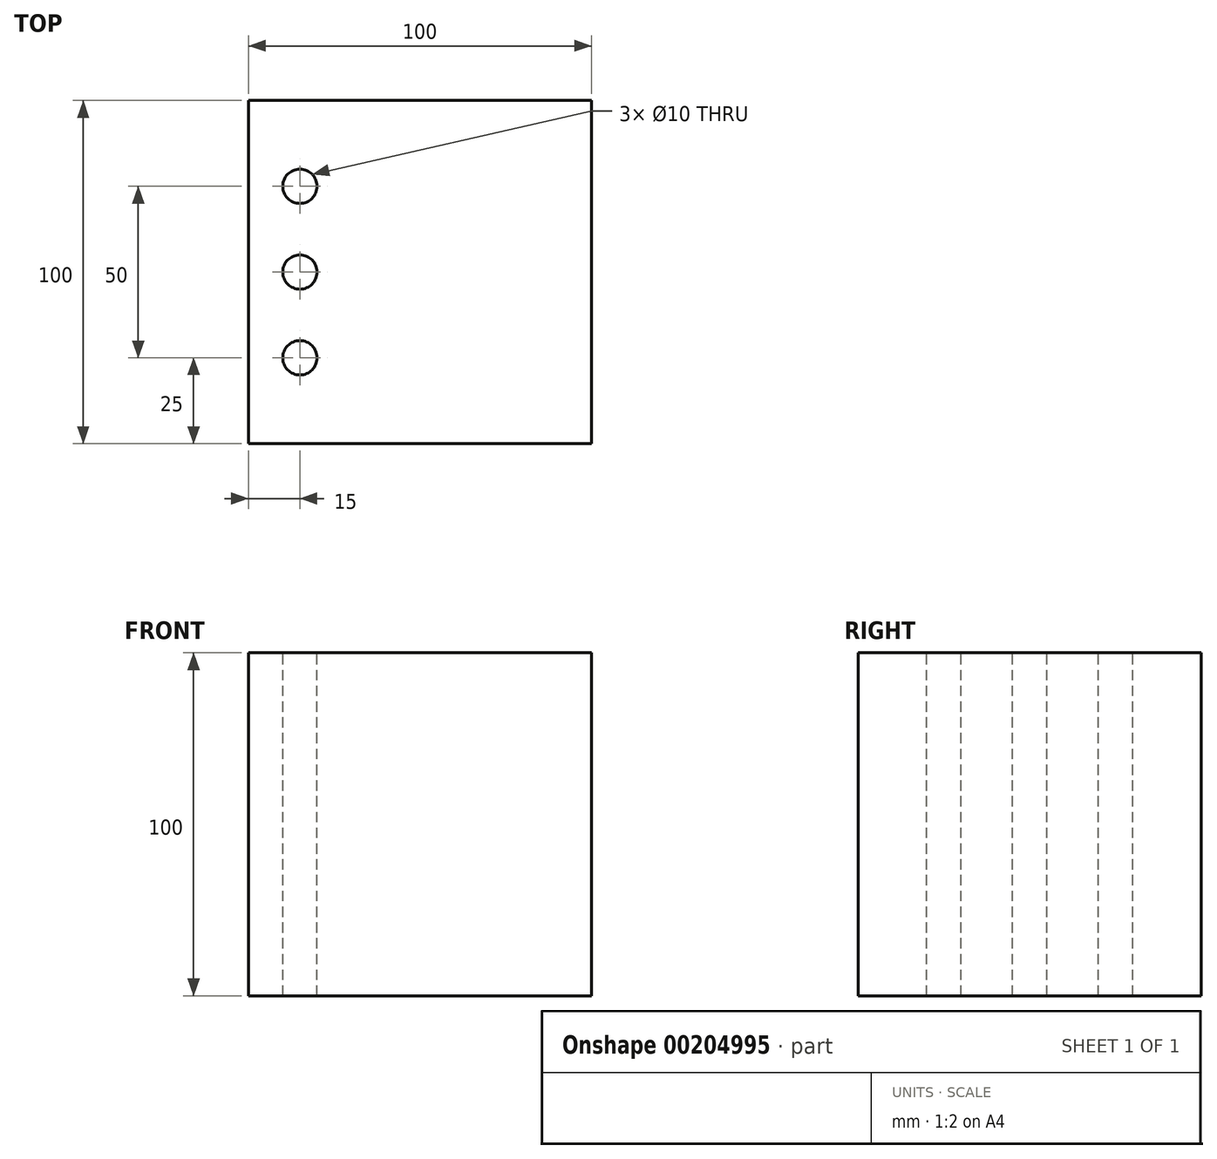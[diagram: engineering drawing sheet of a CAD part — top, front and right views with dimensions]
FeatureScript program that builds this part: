
annotation { "Feature Type Name" : "Feature", "Feature Type Description" : "" }
export const myFeature = defineFeature(function(context is Context, id is Id, definition is map)
    precondition{}
    {
        {
            var Q0;
            Q0=qCreatedBy(makeId("Right.planeOp"),FACE);
            var sketch = newSketch(context, id + "F0", { "sketchPlane" : qUnion([Q0])});
            skLineSegment(sketch, "E0", {"start": v(0, 0) * mm, "end": v(0, 100) * mm});
            skLineSegment(sketch, "E1", {"start": v(0, 100) * mm, "end": v(100, 100) * mm});
            skLineSegment(sketch, "E2", {"start": v(100, 100) * mm, "end": v(100, 0) * mm});
            skLineSegment(sketch, "E3", {"start": v(100, 0) * mm, "end": v(0, 0) * mm});
            skSolve(sketch);
        }
        {
            var Q0;
            Q0=makeQuery(id+"F0.imprint","IMPRINT",FACE,{"disambiguationData":[TD([[makeQuery(id+"F0.imprint","IMPRINT",EDGE,{"derivedFrom":sQuery(id+"F0.wireOp",EDGE,"E0")}),-1.0]])]});
            extrude(context, id + "F1", {"entities" : qUnion([Q0]), "depth" : 100 * mm});
        }
        {
            var Q0;
            Q0=makeQuery(id+"F1.opExtrude","SWEPT_FACE",FACE,{"disambiguationData":[OSD([sQuery(id+"F0.wireOp",EDGE,"E1")])]});
            var sketch = newSketch(context, id + "F2", { "sketchPlane" : qUnion([Q0])});
            skCircle(sketch, "E4", {"center": v(15, 25) * mm, "radius": 5 * mm});
            skCircle(sketch, "E5.2.1.0", {"center": v(142.39, 39.03) * mm, "radius": 5 * mm});
            skCircle(sketch, "E6", {"center": v(15, 50) * mm, "radius": 5 * mm});
            skCircle(sketch, "E7", {"center": v(15, 75) * mm, "radius": 5 * mm});
            skSolve(sketch);
        }
        {
            var Q0;
            Q0 = qSketchRegion(id + "F2", true);
            extrude(context, id + "F3", {"entities" : qUnion([Q0]), "operationType" : NewBodyOperationType.REMOVE, "oppositeDirection" : true, "depth" : 100 * mm});
        }
    });
